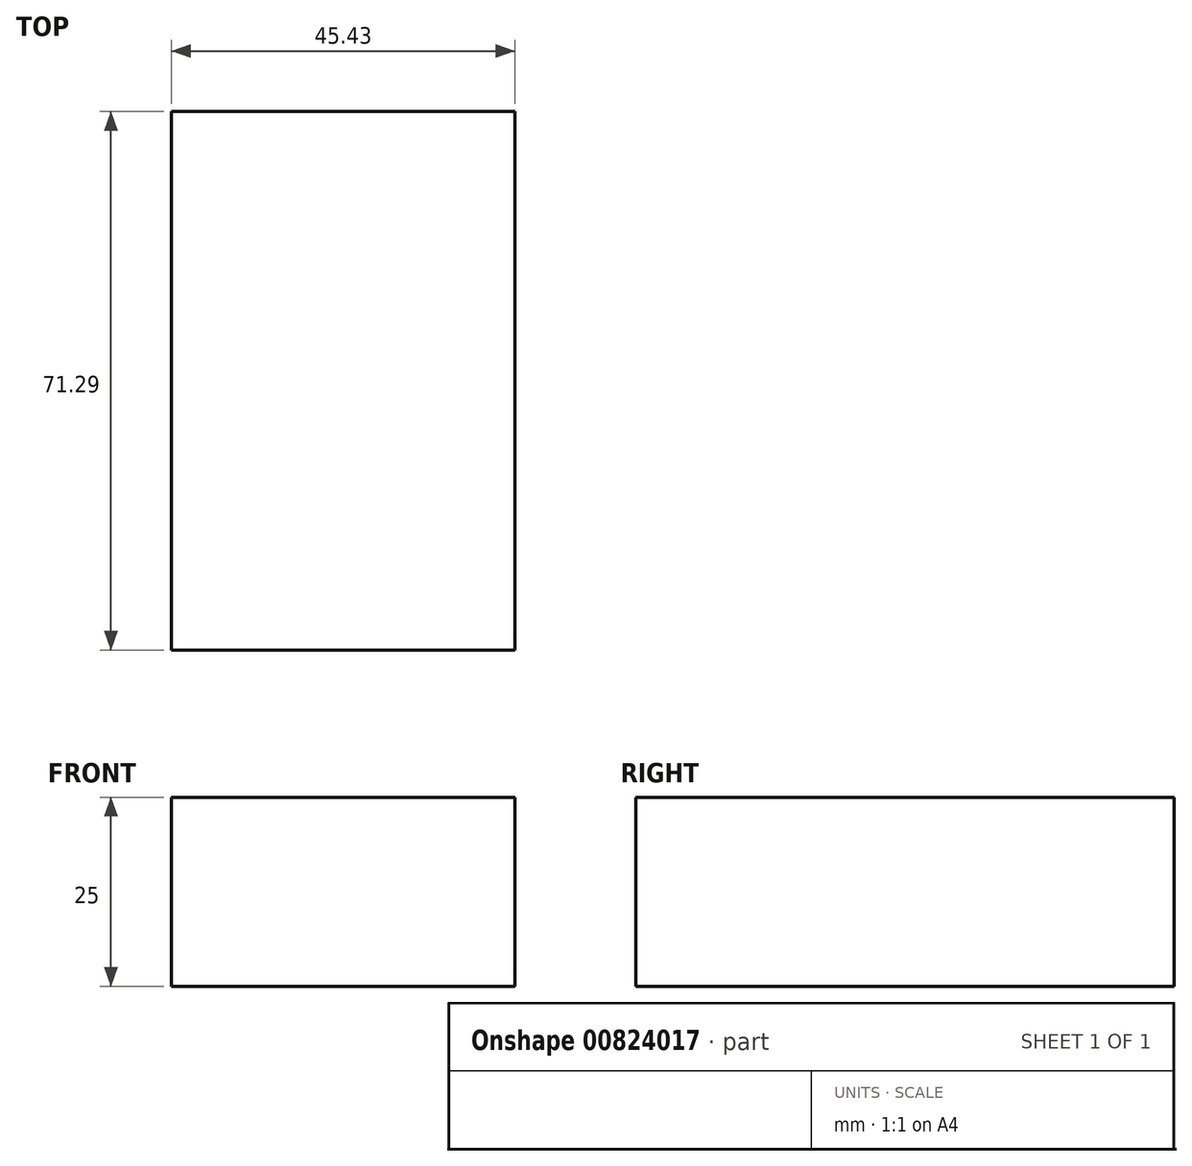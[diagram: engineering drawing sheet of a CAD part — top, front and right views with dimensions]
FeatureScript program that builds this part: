
annotation { "Feature Type Name" : "Feature", "Feature Type Description" : "" }
export const myFeature = defineFeature(function(context is Context, id is Id, definition is map)
    precondition{}
    {
        {
            var Q0;
            Q0=qCreatedBy(makeId("Top.planeOp"),FACE);
            var sketch = newSketch(context, id + "F0", { "sketchPlane" : qUnion([Q0])});
            skLineSegment(sketch, "E0.bottom", {"start": v(28.13, -33.66) * mm, "end": v(-17.3, -33.66) * mm});
            skLineSegment(sketch, "E0.top", {"start": v(28.13, 37.63) * mm, "end": v(-17.3, 37.63) * mm});
            skLineSegment(sketch, "E0.left", {"start": v(28.13, -33.66) * mm, "end": v(28.13, 37.63) * mm});
            skLineSegment(sketch, "E0.right", {"start": v(-17.3, -33.66) * mm, "end": v(-17.3, 37.63) * mm});
            skSolve(sketch);
        }
        {
            var Q0;
            Q0=makeQuery(id+"F0.imprint","IMPRINT",FACE,{"disambiguationData":[TD([[makeQuery(id+"F0.imprint","IMPRINT",EDGE,{"derivedFrom":sQuery(id+"F0.wireOp",EDGE,"E0.bottom")}),-1.0]])]});
            extrude(context, id + "F1", {"entities" : qUnion([Q0]), "depth" : 25 * mm, "offsetDistance" : 25 * mm});
        }
    });
